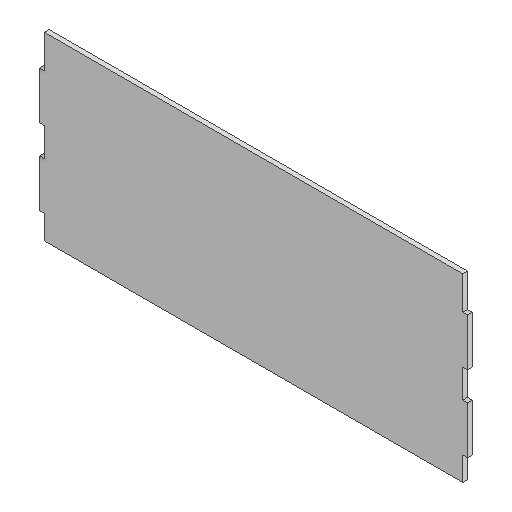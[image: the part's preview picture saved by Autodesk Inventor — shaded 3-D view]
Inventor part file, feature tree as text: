
AUTODESK INVENTOR PART (.ipt)
format: ipt  version: 2022 (Build 260153000, 153)  size: 115,712 bytes
history: native  units: mm
features: reference x8, other x6, extrude x1, sketch x1
ambient origin geometry x8: Origin, YZ Plane, XZ Plane, XY Plane, X Axis, Y Axis, Z Axis, Center Point
bodies: Solid1 (feature_tree)
feature tree (16):
  extrude  "Extrusion1"  Depth=5.0mm
  sketch  "Sketch1"  dims[d0=5.0mm d1=0.0mm d2=5.0mm d3=5.0mm]
  reference  "Reference1"
  reference  "Reference2"
  reference  "Reference3"
  reference  "Reference4"
  reference  "Reference5"
  reference  "Reference6"
  reference  "Reference7"
  reference  "Reference8"
  parser-record x1  (decoder bookkeeping rows leaked as tree rows — omitted from the tree; the rows remain in map.json)
  other  "Ensamble caja.iam"
  other  "Lateral:2"
  other  "Lateral:1"
  other  "Frontal:1"
  other  "Fondo:1"
note: 1 file-system path scrubbed to <path> (originals preserved in map.json)
